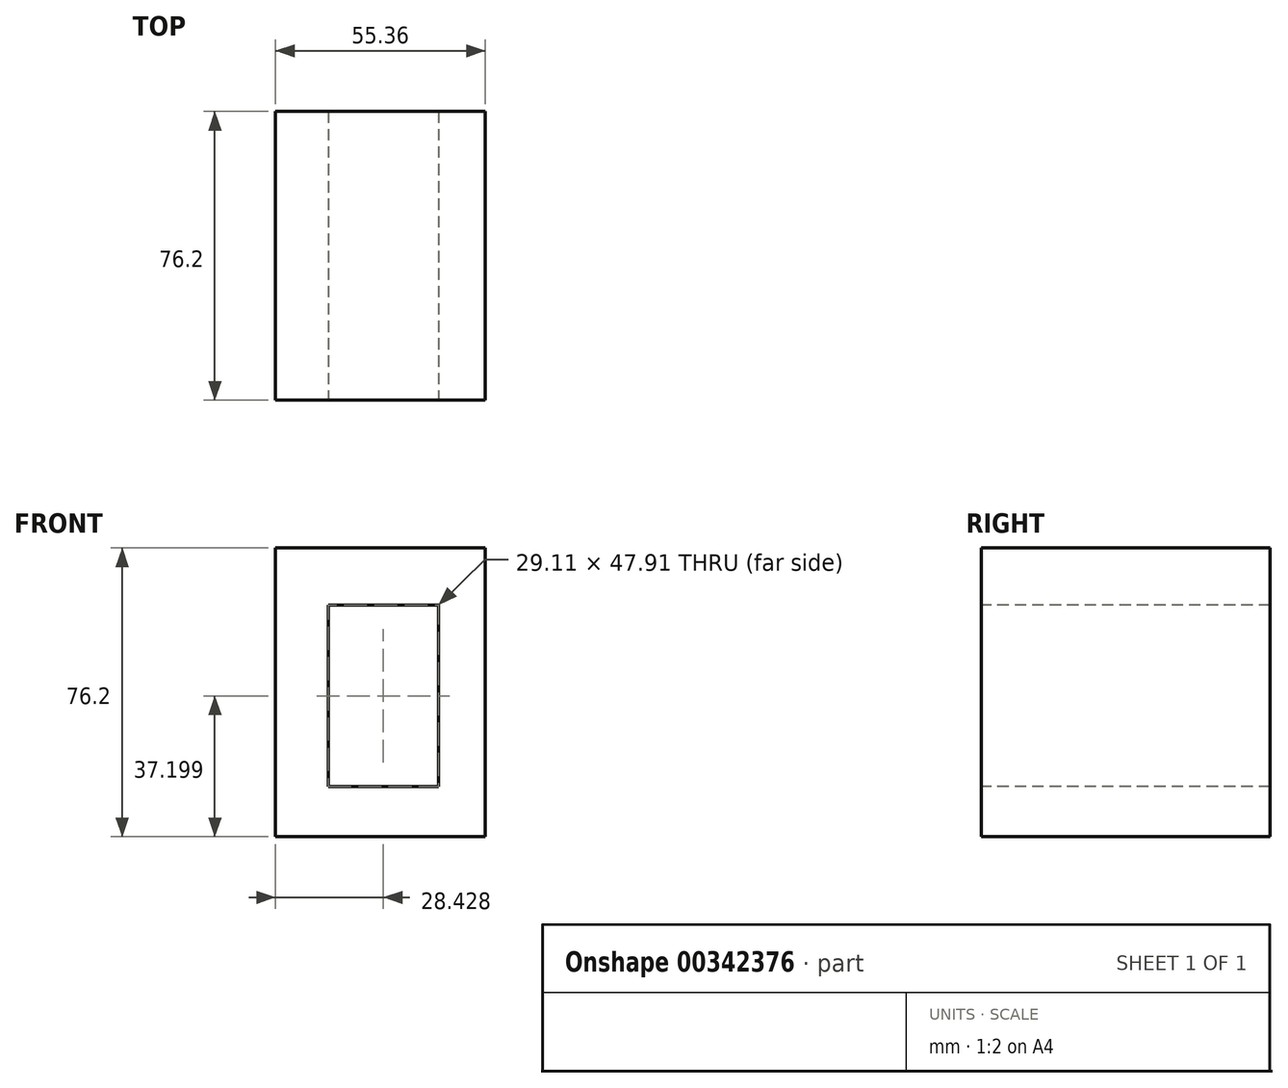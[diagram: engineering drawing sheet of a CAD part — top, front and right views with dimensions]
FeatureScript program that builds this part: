
annotation { "Feature Type Name" : "Feature", "Feature Type Description" : "" }
export const myFeature = defineFeature(function(context is Context, id is Id, definition is map)
    precondition{}
    {
        {
            var Q0;
            Q0=qCreatedBy(makeId("Top.planeOp"),FACE);
            var sketch = newSketch(context, id + "F0", { "sketchPlane" : qUnion([Q0])});
            skLineSegment(sketch, "E0.bottom", {"start": v(0, 0) * mm, "end": v(-55.36, 0) * mm});
            skLineSegment(sketch, "E0.top", {"start": v(0, -59.05) * mm, "end": v(-55.36, -59.05) * mm});
            skLineSegment(sketch, "E0.left", {"start": v(0, 0) * mm, "end": v(0, -59.05) * mm});
            skLineSegment(sketch, "E0.right", {"start": v(-55.36, 0) * mm, "end": v(-55.36, -59.05) * mm});
            skSolve(sketch);
        }
        {
            var Q0;
            Q0 = qSketchRegion(id + "F0", true);
            extrude(context, id + "F1", {"entities" : qUnion([Q0]), "depth" : 76.2 * mm});
        }
        {
            var Q0;
            Q0=makeQuery(id+"F1.opExtrude","SWEPT_FACE",FACE,{"disambiguationData":[OSD([sQuery(id+"F0.wireOp",EDGE,"E0.top")])]});
            extrude(context, id + "F2", {"entities" : qUnion([Q0]), "operationType" : NewBodyOperationType.ADD, "oppositeDirection" : true, "depth" : 76.2 * mm});
        }
        {
            var Q0;
            Q0=makeQuery(id+"F1.opExtrude","SWEPT_FACE",FACE,{"disambiguationData":[OSD([sQuery(id+"F0.wireOp",EDGE,"E0.top")])]});
            var sketch = newSketch(context, id + "F3", { "sketchPlane" : qUnion([Q0])});
            skLineSegment(sketch, "E1.bottom", {"start": v(-12.37, 61.15) * mm, "end": v(-41.49, 61.15) * mm});
            skLineSegment(sketch, "E1.top", {"start": v(-12.37, 13.24) * mm, "end": v(-41.49, 13.24) * mm});
            skLineSegment(sketch, "E1.left", {"start": v(-12.37, 61.15) * mm, "end": v(-12.37, 13.24) * mm});
            skLineSegment(sketch, "E1.right", {"start": v(-41.49, 61.15) * mm, "end": v(-41.49, 13.24) * mm});
            skSolve(sketch);
        }
        {
            var Q0;
            Q0=makeQuery(id+"F3.imprint","IMPRINT",FACE,{"disambiguationData":[TD([[makeQuery(id+"F3.imprint","IMPRINT",EDGE,{"derivedFrom":sQuery(id+"F3.wireOp",EDGE,"E1.bottom")}),1.0]])]});
            extrude(context, id + "F4", {"entities" : qUnion([Q0]), "operationType" : NewBodyOperationType.REMOVE, "endBound" : BoundingType.UP_TO_NEXT, "oppositeDirection" : true, "depth" : 25.4 * mm});
        }
    });
